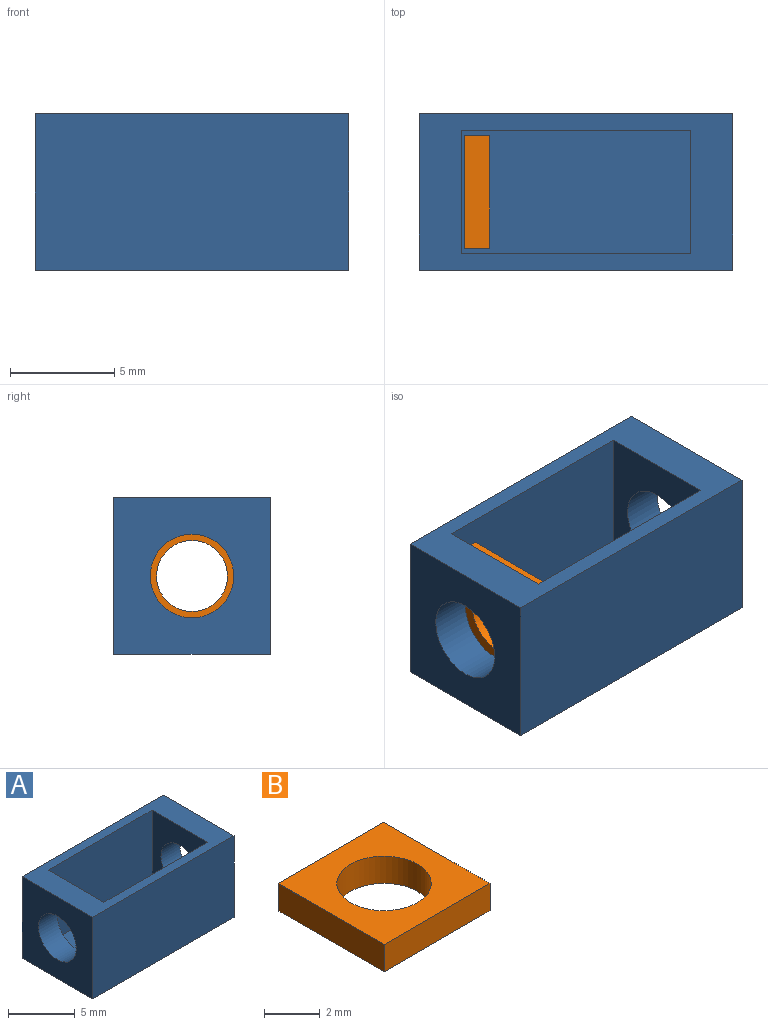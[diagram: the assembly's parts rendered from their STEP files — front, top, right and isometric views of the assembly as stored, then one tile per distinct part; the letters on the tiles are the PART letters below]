
ASSEMBLY  parts=2 mates=1
PART A: 13 faces, bbox 15x7.5x7.5 mm
  f0: cylinder r=2mm len=4mm, axis (-1,0,0), area 25.1mm2, adj f2,f8
  f1: plane 15x7.5mm, normal (0,-1,0), area 112.5mm2, adj f2,f4,f5,f6
  f2: plane 7.5x7.5mm, normal (1,0,0), area 43.7mm2, adj f0,f1,f3,f5,f6
  f3: plane 15x7.5mm, normal (0,1,0), area 112.5mm2, adj f2,f4,f5,f6
  f4: plane 7.5x7.5mm, normal (-1,0,0), area 43.7mm2, adj f1,f3,f5,f6,f7
  f5: plane 15x7.5mm, normal (0,0,1), area 47.6mm2, adj f1,f2,f3,f4,f8,f9,f11,f12
  f6: plane 15x7.5mm, normal (0,0,-1), area 112.5mm2, adj f1,f2,f3,f4
  f7: cylinder r=2mm len=4mm, axis (-1,0,0), area 25.1mm2, adj f4,f9
  f8: plane 6.7x5.9mm, normal (-1,0,0), area 27mm2, adj f0,f5,f10,f11,f12
  f9: plane 6.7x5.9mm, normal (1,0,0), area 27mm2, adj f5,f7,f10,f11,f12
  f10: plane 11x5.9mm, normal (0,0,1), area 64.9mm2, adj f8,f9,f11,f12
  f11: plane 11x6.7mm, normal (0,-1,0), area 73.7mm2, adj f5,f8,f9,f10
  f12: plane 11x6.7mm, normal (0,1,0), area 73.7mm2, adj f5,f8,f9,f10
PART B: 7 faces, bbox 5.4x5.4x1.2 mm
  f0: plane 5.4x1.2mm, normal (0,-1,0), area 6.5mm2, adj f1,f4,f5,f6
  f1: plane 5.4x1.2mm, normal (1,0,0), area 6.5mm2, adj f0,f2,f5,f6
  f2: plane 5.4x1.2mm, normal (0,1,0), area 6.5mm2, adj f1,f4,f5,f6
  f3: cylinder r=1.7mm len=3.4mm, axis (0,0,-1), area 12.8mm2, adj f5,f6
  f4: plane 5.4x1.2mm, normal (-1,0,0), area 6.5mm2, adj f0,f2,f5,f6
  f5: plane 5.4x5.4mm, normal (0,0,1), area 20.1mm2, adj f0,f1,f2,f3,f4
  f6: plane 5.4x5.4mm, normal (0,0,-1), area 20.1mm2, adj f0,f1,f2,f3,f4
PLACE A rot(axis=(0,1,0),0deg) t=(-0.5,11.1,2.8)mm
PLACE B rot(axis=(0,-1,0),90deg) t=(-4.63,42.47,33.9)mm
MATE slider A.f0 <-> B.f3  axis (-1,0,0) through (-8,11.1,6.55)mm
